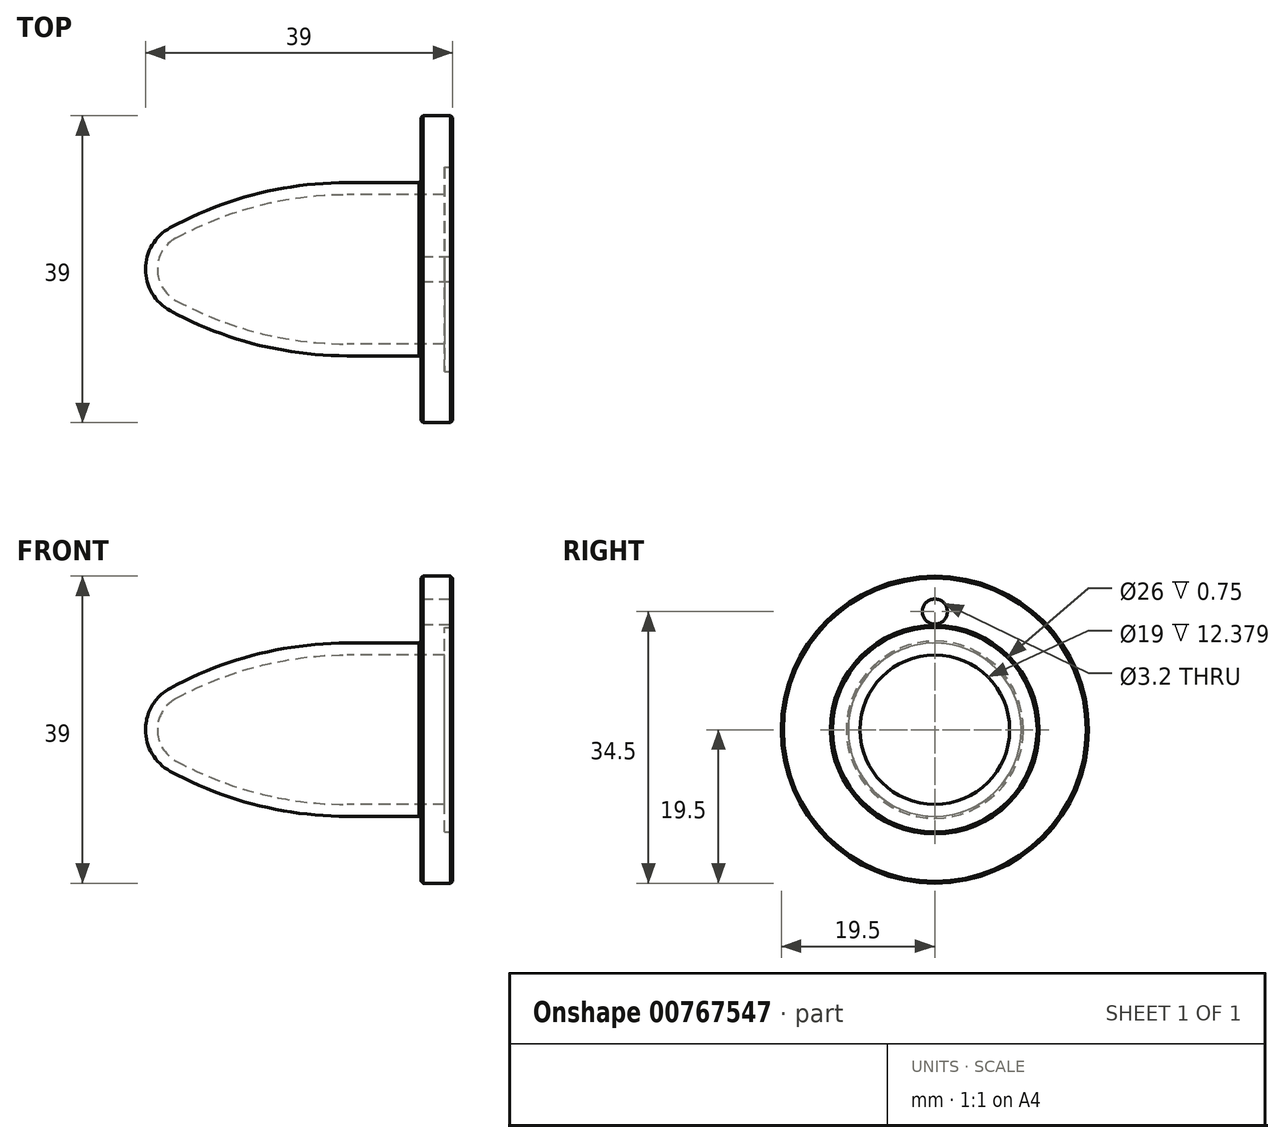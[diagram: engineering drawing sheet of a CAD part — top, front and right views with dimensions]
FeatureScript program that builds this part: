
annotation { "Feature Type Name" : "Feature", "Feature Type Description" : "" }
export const myFeature = defineFeature(function(context is Context, id is Id, definition is map)
    precondition{}
    {
        {
            var Q0;
            Q0=qCreatedBy(makeId("Front.planeOp"),FACE);
            var sketch = newSketch(context, id + "F0", { "sketchPlane" : qUnion([Q0])});
            skLineSegment(sketch, "E0", {"start": v(0, 0) * mm, "end": v(0, 11) * mm});
            skLineSegment(sketch, "E1", {"start": v(0, 11) * mm, "end": v(-13.38, 11) * mm});
            skArc(sketch, "E2", {"start": v(-13.38, 11) * mm, "mid": v(-24.98, 9.54) * mm, "end": v(-35.87, 5.27) * mm});
            skArc(sketch, "E3", {"start": v(-35.87, 5.27) * mm, "mid": v(-38.16, 3.06) * mm, "end": v(-39, 0) * mm});
            skLineSegment(sketch, "E4", {"start": v(-39, 0) * mm, "end": v(0, 0) * mm});
            skSolve(sketch);
        }
        {
            var Q0;
            Q0 = qSketchRegion(id + "F0", true);
            var Q1;
            Q1=sQuery(id+"F0.wireOp",EDGE,"E4");
            revolve(context, id + "F1", {"surfaceOperationType" : NewSurfaceOperationType.NEW, "entities" : qUnion([Q0]), "axis" : qUnion([Q1]), "revolveType" : RevolveType.FULL});
        }
        {
            var Q0;
            Q0=makeQuery(id+"F1.opRevolve","SWEPT_FACE",FACE,{"disambiguationData":[OSD([sQuery(id+"F0.wireOp",EDGE,"E0")])]});
            shell(context, id + "F2", {"entities" : qUnion([Q0]), "thickness" : 1.5 * mm});
        }
        {
            var Q0;
            Q0=qCreatedBy(makeId("Right.planeOp"),FACE);
            var sketch = newSketch(context, id + "F3", { "sketchPlane" : qUnion([Q0])});
            skCircle(sketch, "E5", {"center": v(0, 0) * mm, "radius": 19.5 * mm});
            skCircle(sketch, "E6", {"center": v(0, 0) * mm, "radius": 11 * mm});
            skSolve(sketch);
        }
        {
            var Q0;
            Q0 = qSketchRegion(id + "F3", true);
            extrude(context, id + "F4", {"entities" : qUnion([Q0]), "operationType" : NewBodyOperationType.ADD, "oppositeDirection" : true, "depth" : 4 * mm, "offsetDistance" : 25 * mm});
        }
        {
            var Q0;
            Q0=qCreatedBy(makeId("Right.planeOp"),FACE);
            var sketch = newSketch(context, id + "F5", { "sketchPlane" : qUnion([Q0])});
            skCircle(sketch, "E7", {"center": v(0, 0) * mm, "radius": 13 * mm});
            skSolve(sketch);
        }
        {
            var Q0;
            Q0 = qSketchRegion(id + "F5", true);
            extrude(context, id + "F6", {"entities" : qUnion([Q0]), "operationType" : NewBodyOperationType.REMOVE, "oppositeDirection" : true, "depth" : 1 * mm, "offsetDistance" : 25 * mm});
        }
        {
            var Q0;
            Q0=makeQuery(id+"F4.opExtrude","CAP_FACE",FACE,{"disambiguationData":[OSD([sQuery(id+"F3.wireOp",EDGE,"E5"),sQuery(id+"F3.wireOp",EDGE,"E6")])],"isStart":false});
            var Q1;
            Q1=makeQuery(id+"F4.boolean.opBoolean","MERGE",FACE,{"derivedFrom":[makeQuery(id+"F1.opRevolve","SWEPT_FACE",FACE,{"disambiguationData":[OSD([sQuery(id+"F0.wireOp",EDGE,"E0")])]}),makeQuery(id+"F4.opExtrude","CAP_FACE",FACE,{"disambiguationData":[OSD([sQuery(id+"F3.wireOp",EDGE,"E5"),sQuery(id+"F3.wireOp",EDGE,"E6")])],"isStart":true})]});
            chamfer(context, id + "F7", {"entities" : qUnion([Q0, Q1]), "width" : 0.25 * mm, "tangentPropagation" : true});
        }
        {
            var Q0;
            Q0=qCreatedBy(makeId("Right.planeOp"),FACE);
            var sketch = newSketch(context, id + "F8", { "sketchPlane" : qUnion([Q0])});
            skPoint(sketch, "E8", {"position": v(0, 15) * mm});
            skSolve(sketch);
        }
        {
            var Q0;
            Q0=sQuery(id+"F8.wireOp",VERTEX,"E8");
            var Q1;
            Q1=makeQuery(id+"F1.opRevolve","SWEPT_BODY",BODY,{"disambiguationData":[OSD([sQuery(id+"F0.wireOp",EDGE,"E0"),sQuery(id+"F0.wireOp",EDGE,"E1"),sQuery(id+"F0.wireOp",EDGE,"E2"),sQuery(id+"F0.wireOp",EDGE,"E3"),sQuery(id+"F0.wireOp",EDGE,"E4")])]});
            hole(context, id + "F9", {"style" : HoleStyle.SIMPLE, "endStyle" : HoleEndStyle.THROUGH, "holeDiameter" : 3.2 * mm, "majorDiameter" : 5 * mm, "tappedDepth" : 6 * mm, "tapClearance" : 0, "startFromSketch" : true, "locations" : qUnion([Q0]), "scope" : qUnion([Q1])});
        }
    });
